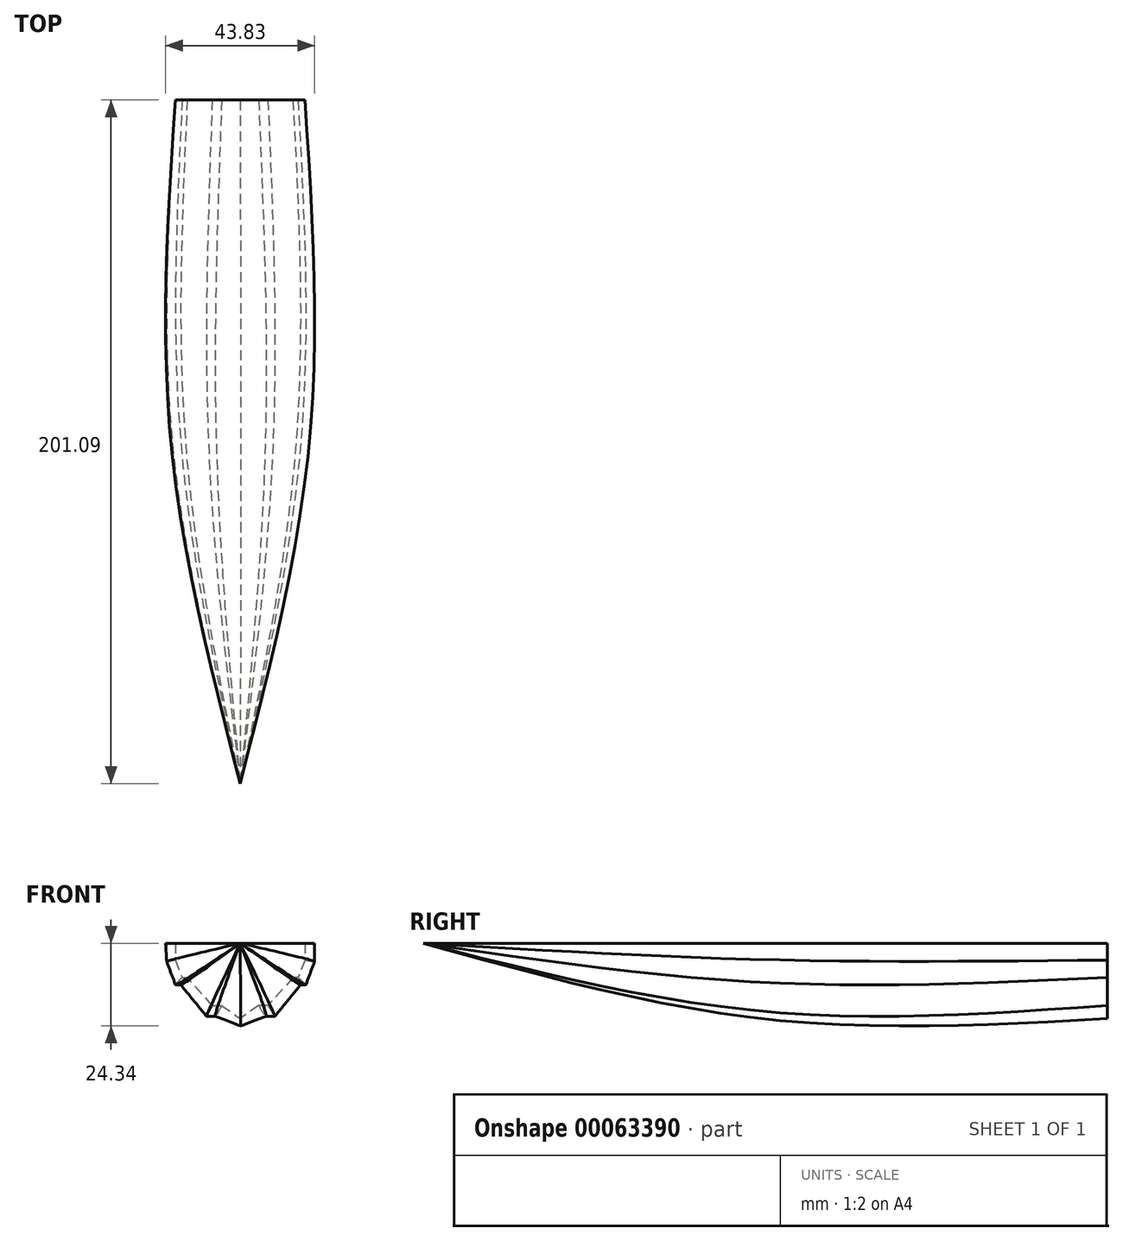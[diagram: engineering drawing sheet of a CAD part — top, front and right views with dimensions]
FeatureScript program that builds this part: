
annotation { "Feature Type Name" : "Feature", "Feature Type Description" : "" }
export const myFeature = defineFeature(function(context is Context, id is Id, definition is map)
    precondition{}
    {
        {
            var Q0;
            Q0=qCreatedBy(makeId("Front.planeOp"),FACE);
            cPlane(context, id + "F0", {"entities" : qUnion([Q0]), "cplaneType" : CPlaneType.OFFSET, "offset" : 50.8 * mm, "width" : 152.4 * mm, "height" : 152.4 * mm});
        }
        {
            var Q0;
            Q0=qCreatedBy(id+"F0.planeOp",FACE);
            cPlane(context, id + "F1", {"entities" : qUnion([Q0]), "cplaneType" : CPlaneType.OFFSET, "offset" : 50.8 * mm, "width" : 152.4 * mm, "height" : 152.4 * mm});
        }
        {
            var Q0;
            Q0=qCreatedBy(id+"F1.planeOp",FACE);
            cPlane(context, id + "F2", {"entities" : qUnion([Q0]), "cplaneType" : CPlaneType.OFFSET, "offset" : 50.8 * mm, "width" : 152.4 * mm, "height" : 152.4 * mm});
        }
        {
            var Q0;
            Q0=qCreatedBy(id+"F2.planeOp",FACE);
            cPlane(context, id + "F3", {"entities" : qUnion([Q0]), "cplaneType" : CPlaneType.OFFSET, "offset" : 50.8 * mm, "width" : 152.4 * mm, "height" : 152.4 * mm});
        }
        {
            var Q0;
            Q0=qCreatedBy(id+"F3.planeOp",FACE);
            cPlane(context, id + "F4", {"entities" : qUnion([Q0]), "cplaneType" : CPlaneType.OFFSET, "offset" : 50.8 * mm, "width" : 152.4 * mm, "height" : 152.4 * mm});
        }
        {
            var Q0;
            Q0=qCreatedBy(id+"F4.planeOp",FACE);
            cPlane(context, id + "F5", {"entities" : qUnion([Q0]), "cplaneType" : CPlaneType.OFFSET, "offset" : 50.8 * mm, "width" : 152.4 * mm, "height" : 152.4 * mm});
        }
        {
            var Q0;
            Q0=qCreatedBy(id+"F5.planeOp",FACE);
            cPlane(context, id + "F6", {"entities" : qUnion([Q0]), "cplaneType" : CPlaneType.OFFSET, "offset" : 50.8 * mm, "width" : 152.4 * mm, "height" : 152.4 * mm});
        }
        {
            var Q0;
            Q0=qCreatedBy(makeId("Top.planeOp"),FACE);
            var sketch = newSketch(context, id + "F7", { "sketchPlane" : qUnion([Q0])});
            skFitSpline(sketch, "E0.MirrorCS", {"points": [v(0, 0) * mm, v(0, -115.25) * mm, v(19.05, -201.1) * mm], "startDerivative": vector(-10.9, -224.4) * mm, "endDerivative": vector(50.38, -176.7) * mm});
            skFitSpline(sketch, "E1.MirrorCS", {"points": [v(38.1, 0) * mm, v(38.1, -115.25) * mm, v(19.05, -201.1) * mm], "startDerivative": vector(10.9, -224.4) * mm, "endDerivative": vector(-50.38, -176.7) * mm});
            skPoint(sketch, "E2", {"position": v(39.32, -101.44) * mm});
            skPoint(sketch, "E3", {"position": v(-1.22, -101.44) * mm});
            skLineSegment(sketch, "E4", {"start": v(38.1, 0) * mm, "end": v(0, 0) * mm});
            skSolve(sketch);
        }
        {
            var Q0;
            Q0=qCreatedBy(makeId("Front.planeOp"),FACE);
            var sketch = newSketch(context, id + "F8", { "sketchPlane" : qUnion([Q0])});
            skPoint(sketch, "E5.0", {"position": v(38.1, 0) * mm});
            skLineSegment(sketch, "E6.0", {"start": v(38.1, 0) * mm, "end": v(19.05, 0) * mm});
            skLineSegment(sketch, "E7", {"start": v(38.1, 0) * mm, "end": v(38.1, -4.97) * mm});
            skLineSegment(sketch, "E8", {"start": v(38.1, -4.97) * mm, "end": v(36.1, -10.09) * mm});
            skLineSegment(sketch, "E9", {"start": v(36.1, -10.09) * mm, "end": v(34.6, -10.09) * mm});
            skLineSegment(sketch, "E10", {"start": v(27.25, -18.3) * mm, "end": v(24.48, -18.3) * mm});
            skLineSegment(sketch, "E11", {"start": v(24.48, -18.3) * mm, "end": v(19.05, -22.13) * mm});
            skLineSegment(sketch, "E12.MirrorCS", {"start": v(13.62, -18.3) * mm, "end": v(19.05, -22.13) * mm});
            skLineSegment(sketch, "E13.MirrorCS", {"start": v(10.85, -18.3) * mm, "end": v(13.62, -18.3) * mm});
            skLineSegment(sketch, "E14.MirrorCS", {"start": v(2, -10.09) * mm, "end": v(3.5, -10.09) * mm});
            skLineSegment(sketch, "E15.MirrorCS", {"start": v(0, -4.97) * mm, "end": v(2, -10.09) * mm});
            skLineSegment(sketch, "E16.MirrorCS", {"start": v(0, 0) * mm, "end": v(0, -4.97) * mm});
            skLineSegment(sketch, "E17", {"start": v(19.05, 0) * mm, "end": v(0, 0) * mm});
            skLineSegment(sketch, "E18", {"start": v(34.6, -10.09) * mm, "end": v(27.25, -18.3) * mm});
            skLineSegment(sketch, "E19", {"start": v(10.85, -18.3) * mm, "end": v(3.5, -10.09) * mm});
            skSolve(sketch);
        }
        {
            var Q0;
            Q0=qCreatedBy(id+"F1.planeOp",FACE);
            var sketch = newSketch(context, id + "F9", { "sketchPlane" : qUnion([Q0])});
            skPoint(sketch, "E20.0", {"position": v(-1.22, 0) * mm});
            skPoint(sketch, "E21.0", {"position": v(39.32, 0) * mm});
            skLineSegment(sketch, "E22.MirrorCS", {"start": v(39.3, 0) * mm, "end": v(39.3, -4.78) * mm});
            skLineSegment(sketch, "E23.MirrorCS", {"start": v(39.3, -4.78) * mm, "end": v(36.83, -11.5) * mm});
            skLineSegment(sketch, "E24.MirrorCS", {"start": v(36.83, -11.5) * mm, "end": v(35.43, -11.5) * mm});
            skLineSegment(sketch, "E25.MirrorCS", {"start": v(28.7, -19.97) * mm, "end": v(26.42, -19.97) * mm});
            skLineSegment(sketch, "E26.MirrorCS", {"start": v(26.42, -19.97) * mm, "end": v(18.94, -22.23) * mm});
            skLineSegment(sketch, "E27.MirrorCS", {"start": v(12.04, -19.97) * mm, "end": v(19.52, -22.23) * mm});
            skLineSegment(sketch, "E28.MirrorCS", {"start": v(9.76, -19.97) * mm, "end": v(12.04, -19.97) * mm});
            skLineSegment(sketch, "E29.MirrorCS", {"start": v(1.64, -11.5) * mm, "end": v(3.03, -11.5) * mm});
            skLineSegment(sketch, "E30.MirrorCS", {"start": v(-0.84, -4.78) * mm, "end": v(1.64, -11.5) * mm});
            skLineSegment(sketch, "E31", {"start": v(-1.22, 0) * mm, "end": v(39.32, 0) * mm});
            skLineSegment(sketch, "E32", {"start": v(-1.22, 0) * mm, "end": v(-0.84, -4.78) * mm});
            skLineSegment(sketch, "E33", {"start": v(35.43, -11.5) * mm, "end": v(28.7, -19.97) * mm});
            skLineSegment(sketch, "E34", {"start": v(9.76, -19.97) * mm, "end": v(3.03, -11.5) * mm});
            skSolve(sketch);
        }
        {
            var Q0;
            {var subQ1=sQuery(id+"F8.wireOp",EDGE,"E6.0");Q0=makeQuery(id+"F8.imprint","IMPRINT",FACE,{"disambiguationData":[TD([[makeQuery(id+"F8.imprint","IMPRINT",EDGE,{"derivedFrom":subQ1}),1.0]])]});}
            var Q1;
            {var subQ5=sQuery(id+"F9.wireOp",EDGE,"E22.MirrorCS");Q1=makeQuery(id+"F9.imprint","IMPRINT",FACE,{"disambiguationData":[TD([[makeQuery(id+"F9.imprint","IMPRINT",EDGE,{"derivedFrom":subQ5}),-1.0]])]});}
            var Q2;
            Q2=sQuery(id+"F7.wireOp",VERTEX,"E0.MirrorCS.end");
            loft(context, id + "F10", {"sheetProfilesArray" : [{ "sheetProfileEntities" : qUnion([Q0]) }, { "sheetProfileEntities" : qUnion([Q1]) }, { "sheetProfileEntities" : qUnion([Q2]) }]});
        }
    });
